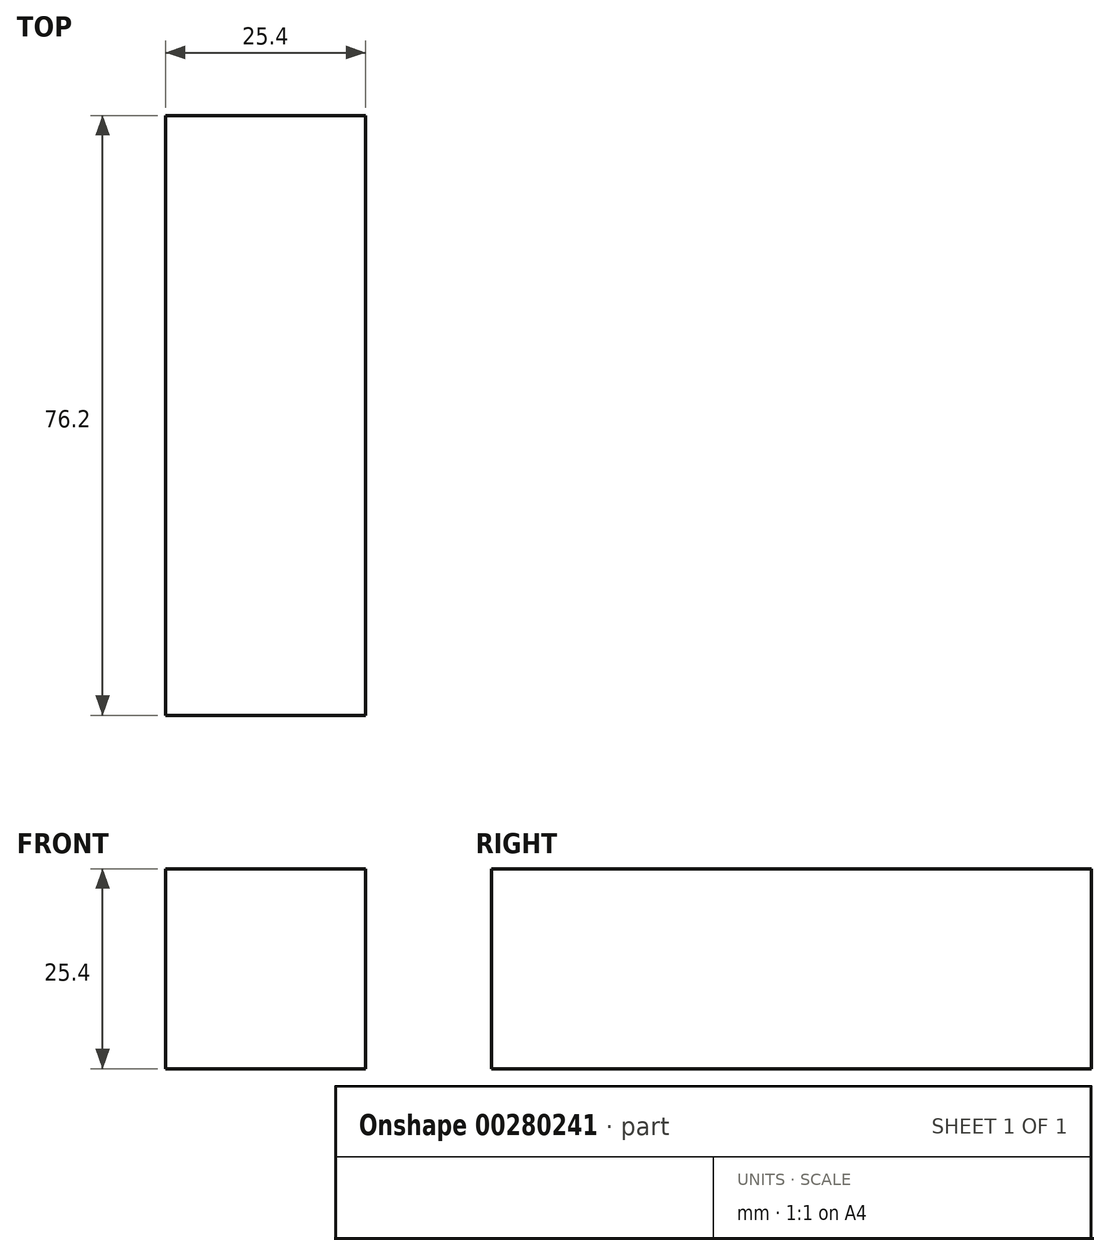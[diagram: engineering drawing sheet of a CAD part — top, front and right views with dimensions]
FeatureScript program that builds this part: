
annotation { "Feature Type Name" : "Feature", "Feature Type Description" : "" }
export const myFeature = defineFeature(function(context is Context, id is Id, definition is map)
    precondition{}
    {
        {
            var Q0;
            Q0=qCreatedBy(makeId("Front.planeOp"),FACE);
            var sketch = newSketch(context, id + "F0", { "sketchPlane" : qUnion([Q0])});
            skLineSegment(sketch, "E0.bottom", {"start": v(0, 0) * mm, "end": v(25.4, 0) * mm});
            skLineSegment(sketch, "E0.top", {"start": v(0, 25.4) * mm, "end": v(25.4, 25.4) * mm});
            skLineSegment(sketch, "E0.left", {"start": v(0, 0) * mm, "end": v(0, 25.4) * mm});
            skLineSegment(sketch, "E0.right", {"start": v(25.4, 0) * mm, "end": v(25.4, 25.4) * mm});
            skSolve(sketch);
        }
        {
            var Q0;
            Q0=makeQuery(id+"F0.imprint","IMPRINT",FACE,{"disambiguationData":[TD([[makeQuery(id+"F0.imprint","IMPRINT",EDGE,{"derivedFrom":sQuery(id+"F0.wireOp",EDGE,"E0.bottom")}),1.0]])]});
            extrude(context, id + "F1", {"entities" : qUnion([Q0]), "depth" : 76.2 * mm});
        }
    });
